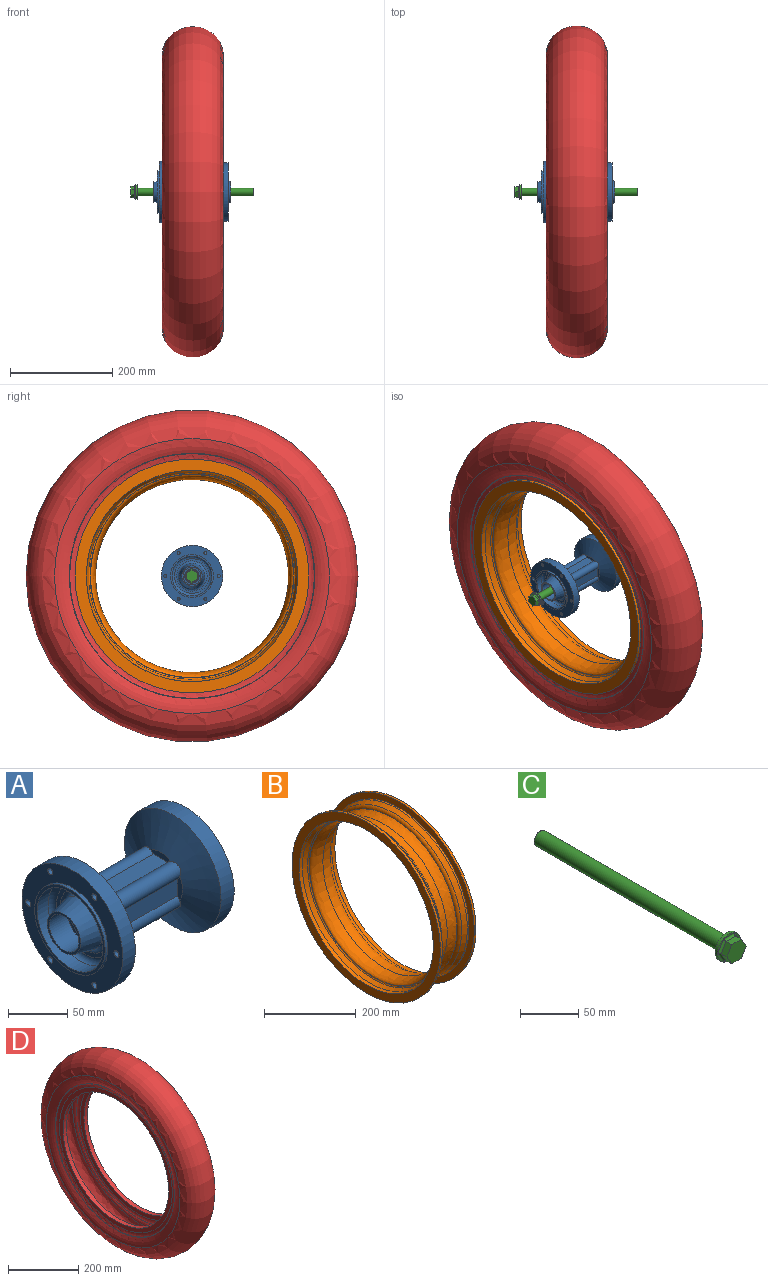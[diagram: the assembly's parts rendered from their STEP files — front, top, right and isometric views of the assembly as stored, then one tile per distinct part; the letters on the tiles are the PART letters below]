
ASSEMBLY  parts=4 mates=3
PART A: 49 faces, bbox 150x120x120 mm
  f0: cylinder r=57.5mm len=115mm, axis (1,0,0), area 5602.4mm2, adj f8,f48
  f1: cylinder r=39mm len=78mm, axis (1,0,0), area 2450.4mm2, adj f21,f48
  f2: plane 120x120mm, normal (1,0,0), area 922.8mm2, adj f13,f37
  f3: plane 75x17.51mm, normal (0,-1,0), area 1313.3mm2, adj f4,f5,f6,f7
  f4: cylinder r=8mm len=77.88mm, axis (1,0,0), area 2041.6mm2, adj f3,f5,f7,f8,f9,f10,f11,f40
  f5: plane 25.72x6.1mm, normal (1,0,0), area 114.9mm2, adj f3,f4,f6,f40
  f6: cylinder r=8mm len=77.88mm, axis (1,0,0), area 2041.6mm2, adj f3,f5,f7,f8,f12,f14,f15,f40
  f7: plane 25.72x6.1mm, normal (-1,0,0), area 114.9mm2, adj f3,f4,f6,f8
  f8: cone r=26.09mm half-angle=65.2deg, axis (1,0,0), area 8945.1mm2, adj f0,f4,f6,f7,f9,f14,f16,f17
  f9: plane 25.72x6.1mm, normal (-1,0,0), area 114.9mm2, adj f4,f8,f10,f16
  f10: plane 75x17.51mm, normal (0,0,1), area 1313.3mm2, adj f4,f9,f11,f16
  f11: plane 25.72x6.1mm, normal (1,0,0), area 114.9mm2, adj f4,f10,f16,f40
  f12: plane 25.72x6.1mm, normal (1,0,0), area 114.9mm2, adj f6,f15,f17,f40
  f13: cylinder r=57.5mm len=115mm, axis (1,0,0), area 183.1mm2, adj f2,f40
  f14: plane 25.72x6.1mm, normal (-1,0,0), area 114.9mm2, adj f6,f8,f15,f17
  f15: plane 75x17.51mm, normal (0,0,-1), area 1313.3mm2, adj f6,f12,f14,f17
  f16: cylinder r=8mm len=77.88mm, axis (1,0,0), area 2041.6mm2, adj f8,f9,f10,f11,f18,f19,f20,f40
  f17: cylinder r=8mm len=77.88mm, axis (1,0,0), area 2041.6mm2, adj f8,f12,f14,f15,f18,f19,f20,f40
  f18: plane 25.72x6.1mm, normal (1,0,0), area 114.9mm2, adj f16,f17,f20,f40
  f19: plane 25.72x6.1mm, normal (-1,0,0), area 114.9mm2, adj f8,f16,f17,f20
  f20: plane 75x17.51mm, normal (0,1,0), area 1313.3mm2, adj f16,f17,f18,f19
  f21: torus R=34mm, axis (1,0,0), area 1834.9mm2, adj f1,f22
  f22: plane 68x68mm, normal (1,0,0), area 884.1mm2, adj f21,f23
  f23: torus R=29.57mm, axis (1,0,0), area 1127.8mm2, adj f22,f24
  f24: cone r=21mm half-angle=12.9deg, axis (-1,0,0), area 2374.3mm2, adj f23,f25
  f25: plane 42x42mm, normal (1,0,0), area 423.3mm2, adj f24,f26
  f26: cylinder r=17.5mm len=35mm, axis (1,0,0), area 1869.2mm2, adj f25,f27
  f27: plane 35x35mm, normal (1,0,0), area 785.4mm2, adj f26,f28
  f28: cylinder r=7.5mm len=111mm, axis (1,0,0), area 5230.8mm2, adj f27,f29
  f29: plane 35x35mm, normal (-1,0,0), area 785.4mm2, adj f28,f30
  f30: cylinder r=17.5mm len=35mm, axis (1,0,0), area 2419mm2, adj f29,f31
  f31: plane 39.7x39.7mm, normal (-1,0,0), area 276mm2, adj f30,f32
  f32: cone r=21mm half-angle=12.9deg, axis (1,0,0), area 3032.7mm2, adj f31,f33
  f33: torus R=29.57mm, axis (1,0,0), area 1127.8mm2, adj f32,f34
  f34: plane 68x68mm, normal (-1,0,0), area 884.1mm2, adj f33,f35
  f35: torus R=34mm, axis (1,0,0), area 1834.9mm2, adj f34,f36
  f36: cylinder r=39mm len=78mm, axis (1,0,0), area 3185.6mm2, adj f35,f47
  f37: cylinder r=60mm len=120mm, axis (1,0,0), area 5654.9mm2, adj f2,f39
  f38: cylinder r=42mm len=84mm, axis (1,0,0), area 791.7mm2, adj f39,f47
  f39: plane 120x120mm, normal (-1,0,0), area 5598.3mm2, adj f37,f38,f41,f42,f43,f44,f45,f46
  f40: cone r=26.09mm half-angle=65.2deg, axis (-1,0,0), area 8757.9mm2, adj f4,f5,f6,f11,f12,f13,f16,f17
  f41: cylinder r=3mm len=18.48mm, axis (1,0,0), area 335.2mm2, adj f39,f40
  f42: cylinder r=3mm len=18.48mm, axis (1,0,0), area 335.2mm2, adj f39,f40
  f43: cylinder r=3mm len=18.48mm, axis (1,0,0), area 335.2mm2, adj f39,f40
  f44: cylinder r=3mm len=18.48mm, axis (1,0,0), area 335.2mm2, adj f39,f40
  f45: cylinder r=3mm len=19.08mm, axis (1,0,0), area 333.8mm2, adj f39,f40
  f46: cylinder r=3mm len=19.08mm, axis (1,0,0), area 333.8mm2, adj f39,f40
  f47: plane 84x84mm, normal (-1,0,0), area 763.4mm2, adj f36,f38
  f48: plane 115x115mm, normal (1,0,0), area 5608.5mm2, adj f0,f1
PART B: 24 faces, bbox 110x457.2x457.2 mm
  f0: plane 457.2x457.2mm, normal (1,0,0), area 30078.9mm2, adj f11,f13
  f1: plane 457.2x457.2mm, normal (-1,0,0), area 30078.9mm2, adj f2,f12
  f2: cylinder r=206.6mm len=413.2mm, axis (1,0,0), area 12857.2mm2, adj f1,f3
  f3: cone r=202.31mm half-angle=20deg, axis (-1,0,0), area 16121.1mm2, adj f2,f4
  f4: torus R=199.02mm, axis (1,0,0), area 5397.7mm2, adj f3,f5
  f5: plane 398.04x398.04mm, normal (-1,0,0), area 523.4mm2, adj f4,f6
  f6: revolved ~397.2x397.2mm, area 41272mm2, adj f5,f10
  f7: torus R=199.02mm, axis (1,0,0), area 5397.7mm2, adj f8,f9
  f8: plane 398.04x398.04mm, normal (1,0,0), area 523.4mm2, adj f7,f10
  f9: cone r=202.31mm half-angle=20deg, axis (1,0,0), area 16121.1mm2, adj f7,f11
  f10: revolved ~397.2x397.2mm, area 41272mm2, adj f6,f8
  f11: cylinder r=206.6mm len=413.2mm, axis (1,0,0), area 12857.2mm2, adj f0,f9
  f12: cylinder r=228.6mm len=457.2mm, axis (1,0,0), area 8618mm2, adj f1,f23
  f13: cylinder r=228.6mm len=457.2mm, axis (1,0,0), area 8618mm2, adj f0,f14
  f14: plane 457.2x457.2mm, normal (-1,0,0), area 22177.1mm2, adj f13,f15
  f15: cylinder r=212.6mm len=425.2mm, axis (1,0,0), area 6629mm2, adj f14,f16
  f16: cone r=207.95mm half-angle=20deg, axis (1,0,0), area 17977.7mm2, adj f15,f17
  f17: torus R=199.02mm, axis (1,0,0), area 14214.2mm2, adj f16,f18
  f18: revolved ~399.11x399.11mm, area 31782.7mm2, adj f17,f19
  f19: revolved ~399.11x399.11mm, area 31782.7mm2, adj f18,f20
  f20: torus R=199.02mm, axis (1,0,0), area 14214.2mm2, adj f19,f21
  f21: cone r=207.95mm half-angle=20deg, axis (-1,0,0), area 17977.7mm2, adj f20,f22
  f22: cylinder r=212.6mm len=425.2mm, axis (1,0,0), area 6629mm2, adj f21,f23
  f23: plane 457.2x457.2mm, normal (1,0,0), area 22177.1mm2, adj f12,f22
PART C: 18 faces, bbox 28x239x28 mm
  f0: cylinder r=7.5mm len=227mm, axis (0,1,0), area 10697.1mm2, adj f1,f3
  f1: plane 15x15mm, normal (0,1,0), area 176.7mm2, adj f0
  f2: cylinder r=14mm len=28mm, axis (0,-1,0), area 263.9mm2, adj f3,f4
  f3: plane 28x28mm, normal (0,1,0), area 439mm2, adj f0,f2
  f4: plane 28x28mm, normal (0,-1,0), area 116.9mm2, adj f2,f12,f13,f14,f15,f16,f17
  f5: plane 23.09x20mm, normal (0,-1,0), area 346.4mm2, adj f6,f7,f8,f9,f10,f11
  f6: plane 10x7mm, normal (-0.87,0,-0.5), area 80.8mm2, adj f5,f7,f11,f15
  f7: plane 10x7mm, normal (-0.87,0,0.5), area 80.8mm2, adj f5,f6,f8,f17
  f8: plane 11.55x7mm, normal (0,0,1), area 80.8mm2, adj f5,f7,f9,f16
  f9: plane 10x7mm, normal (0.87,0,0.5), area 80.8mm2, adj f5,f8,f10,f14
  f10: plane 10x7mm, normal (0.87,0,-0.5), area 80.8mm2, adj f5,f9,f11,f12
  f11: plane 11.55x7mm, normal (0,0,-1), area 80.8mm2, adj f5,f6,f10,f13
  f12: cylinder r=2mm len=13mm, axis (-0.5,0,-0.87), area 38.9mm2, adj f4,f10,f13,f14
  f13: cylinder r=2mm len=13.86mm, axis (-1,0,0), area 38.9mm2, adj f4,f11,f12,f15
  f14: cylinder r=2mm len=13mm, axis (0.5,0,-0.87), area 38.9mm2, adj f4,f9,f12,f16
  f15: cylinder r=2mm len=13mm, axis (-0.5,0,0.87), area 38.9mm2, adj f4,f6,f13,f17
  f16: cylinder r=2mm len=13.86mm, axis (1,0,0), area 38.9mm2, adj f4,f8,f14,f17
  f17: cylinder r=2mm len=13mm, axis (0.5,0,0.87), area 38.9mm2, adj f4,f7,f15,f16
PART D: 20 faces, bbox 120x649.2x649.2 mm
  f0: cylinder r=212.6mm len=425.2mm, axis (1,0,0), area 18701.3mm2, adj f16,f19
  f1: torus R=227.18mm, axis (1,0,0), area 29175.6mm2, adj f2,f16
  f2: cone r=245.97mm half-angle=61.2deg, axis (1,0,0), area 1536.8mm2, adj f1,f3
  f3: torus R=269.01mm, axis (1,0,0), area 37175.4mm2, adj f2,f4
  f4: revolved ~618.74x618.74mm, area 256119.8mm2, adj f3,f5
  f5: torus R=269.01mm, axis (1,0,0), area 37175.4mm2, adj f4,f6
  f6: cone r=245.97mm half-angle=61.2deg, axis (-1,0,0), area 1536.8mm2, adj f5,f7
  f7: torus R=227.18mm, axis (1,0,0), area 29175.6mm2, adj f6,f17
  f8: cylinder r=212.6mm len=425.2mm, axis (1,0,0), area 18701.3mm2, adj f17,f18
  f9: torus R=227.18mm, axis (1,0,0), area 18430.1mm2, adj f10,f18
  f10: cone r=239.23mm half-angle=61.2deg, axis (-1,0,0), area 1494.7mm2, adj f9,f11
  f11: torus R=269.01mm, axis (1,0,0), area 47836.3mm2, adj f10,f12
  f12: revolved ~649.2x649.2mm, area 348230.6mm2, adj f11,f13
  f13: torus R=269.01mm, axis (1,0,0), area 47836.3mm2, adj f12,f14
  f14: cone r=239.23mm half-angle=61.2deg, axis (1,0,0), area 1494.7mm2, adj f13,f15
  f15: torus R=227.18mm, axis (1,0,0), area 18430.1mm2, adj f14,f19
  f16: plane 454.36x454.36mm, normal (-1,0,0), area 20141.8mm2, adj f0,f1
  f17: plane 454.36x454.36mm, normal (1,0,0), area 20141.8mm2, adj f7,f8
  f18: plane 454.36x454.36mm, normal (-1,0,0), area 20141.8mm2, adj f8,f9
  f19: plane 454.36x454.36mm, normal (1,0,0), area 20141.8mm2, adj f0,f15
PLACE A t=(401.35,166.21,-280.11)mm
PLACE B t=(399.85,166.21,-280.11)mm
PLACE C rot(axis=(0.58,0.58,-0.58),120deg) t=(517.85,166.21,-280.11)mm
PLACE D t=(399.85,166.21,-280.11)mm
MATE fastened C.f0 <-> A.f0  axis (1,0,0) through (290.85,166.21,-280.11)mm
MATE fastened A.f0 <-> B.f2  axis (-1,0,0) through (330.85,166.21,-280.11)mm
MATE fastened D.f0 <-> B.f2  axis (1,0,0) through (448.85,166.21,-280.11)mm
